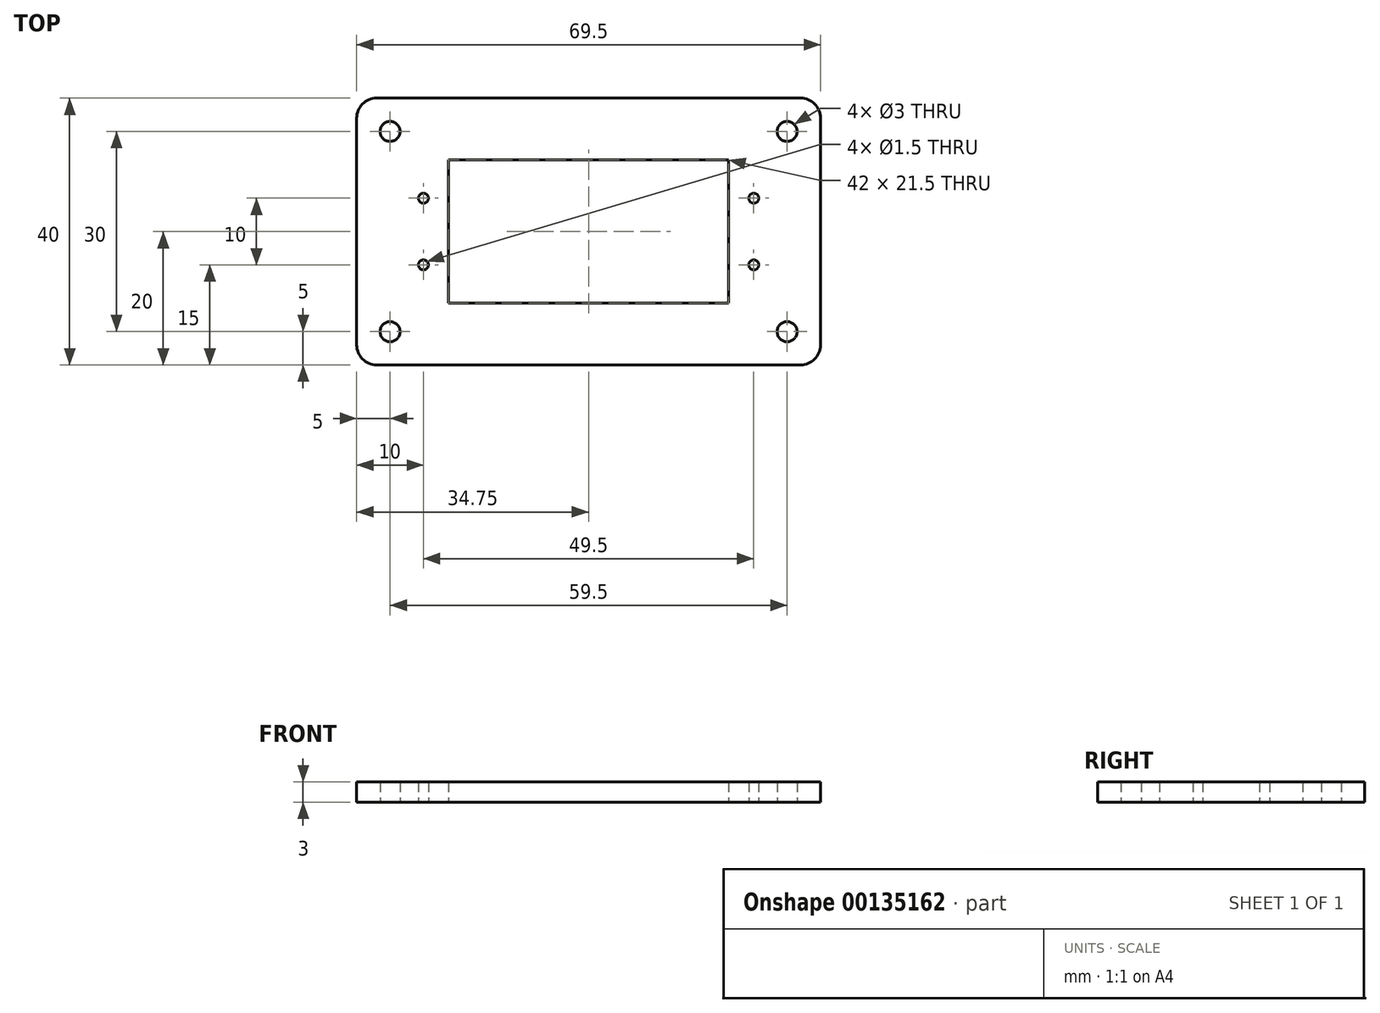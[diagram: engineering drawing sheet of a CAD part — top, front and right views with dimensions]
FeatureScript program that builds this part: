
annotation { "Feature Type Name" : "Feature", "Feature Type Description" : "" }
export const myFeature = defineFeature(function(context is Context, id is Id, definition is map)
    precondition{}
    {
        {
            var Q0;
            Q0=qCreatedBy(makeId("Top.planeOp"),FACE);
            var sketch = newSketch(context, id + "F0", { "sketchPlane" : qUnion([Q0])});
            skLineSegment(sketch, "E0.bottom", {"start": v(21, -10.75) * mm, "end": v(-21, -10.75) * mm});
            skLineSegment(sketch, "E0.top", {"start": v(21, 10.75) * mm, "end": v(-21, 10.75) * mm});
            skLineSegment(sketch, "E0.left", {"start": v(21, -10.75) * mm, "end": v(21, 10.75) * mm});
            skLineSegment(sketch, "E0.right", {"start": v(-21, -10.75) * mm, "end": v(-21, 10.75) * mm});
            skPoint(sketch, "E0.middle", {"position": v(0, 0) * mm});
            skLineSegment(sketch, "E1.bottom", {"start": v(24.75, -5) * mm, "end": v(-24.75, -5) * mm, "construction": true});
            skLineSegment(sketch, "E1.top", {"start": v(24.75, 5) * mm, "end": v(-24.75, 5) * mm, "construction": true});
            skLineSegment(sketch, "E1.left", {"start": v(24.75, -5) * mm, "end": v(24.75, 5) * mm, "construction": true});
            skLineSegment(sketch, "E1.right", {"start": v(-24.75, -5) * mm, "end": v(-24.75, 5) * mm, "construction": true});
            skLineSegment(sketch, "E2.bottom", {"start": v(34.75, -20) * mm, "end": v(-34.75, -20) * mm});
            skLineSegment(sketch, "E2.top", {"start": v(34.75, 20) * mm, "end": v(-34.75, 20) * mm});
            skLineSegment(sketch, "E2.left", {"start": v(34.75, -20) * mm, "end": v(34.75, 20) * mm});
            skLineSegment(sketch, "E2.right", {"start": v(-34.75, -20) * mm, "end": v(-34.75, 20) * mm});
            skLineSegment(sketch, "E3.bottom", {"start": v(-34.75, 20) * mm, "end": v(-29.75, 20) * mm, "construction": true});
            skLineSegment(sketch, "E3.top", {"start": v(-34.75, 15) * mm, "end": v(-29.75, 15) * mm, "construction": true});
            skLineSegment(sketch, "E3.left", {"start": v(-34.75, 20) * mm, "end": v(-34.75, 15) * mm, "construction": true});
            skLineSegment(sketch, "E3.right", {"start": v(-29.75, 20) * mm, "end": v(-29.75, 15) * mm, "construction": true});
            skLineSegment(sketch, "E4.bottom", {"start": v(34.75, 20) * mm, "end": v(29.75, 20) * mm, "construction": true});
            skLineSegment(sketch, "E4.top", {"start": v(34.75, 15) * mm, "end": v(29.75, 15) * mm, "construction": true});
            skLineSegment(sketch, "E4.left", {"start": v(34.75, 20) * mm, "end": v(34.75, 15) * mm, "construction": true});
            skLineSegment(sketch, "E4.right", {"start": v(29.75, 20) * mm, "end": v(29.75, 15) * mm, "construction": true});
            skLineSegment(sketch, "E5.bottom", {"start": v(-34.75, -20) * mm, "end": v(-29.75, -20) * mm, "construction": true});
            skLineSegment(sketch, "E5.top", {"start": v(-34.75, -15) * mm, "end": v(-29.75, -15) * mm, "construction": true});
            skLineSegment(sketch, "E5.left", {"start": v(-34.75, -20) * mm, "end": v(-34.75, -15) * mm, "construction": true});
            skLineSegment(sketch, "E5.right", {"start": v(-29.75, -20) * mm, "end": v(-29.75, -15) * mm, "construction": true});
            skLineSegment(sketch, "E6.bottom", {"start": v(34.75, -20) * mm, "end": v(29.75, -20) * mm, "construction": true});
            skLineSegment(sketch, "E6.top", {"start": v(34.75, -15) * mm, "end": v(29.75, -15) * mm, "construction": true});
            skLineSegment(sketch, "E6.left", {"start": v(34.75, -20) * mm, "end": v(34.75, -15) * mm, "construction": true});
            skLineSegment(sketch, "E6.right", {"start": v(29.75, -20) * mm, "end": v(29.75, -15) * mm, "construction": true});
            skCircle(sketch, "E7", {"center": v(-29.75, 15) * mm, "radius": 1.5 * mm});
            skCircle(sketch, "E8", {"center": v(29.75, 15) * mm, "radius": 1.5 * mm});
            skCircle(sketch, "E9", {"center": v(-29.75, -15) * mm, "radius": 1.5 * mm});
            skCircle(sketch, "E10", {"center": v(29.75, -15) * mm, "radius": 1.5 * mm});
            skCircle(sketch, "E11", {"center": v(-24.75, 5) * mm, "radius": 0.75 * mm});
            skCircle(sketch, "E12", {"center": v(24.75, 5) * mm, "radius": 0.75 * mm});
            skCircle(sketch, "E13", {"center": v(-24.75, -5) * mm, "radius": 0.75 * mm});
            skCircle(sketch, "E14", {"center": v(24.75, -5) * mm, "radius": 0.75 * mm});
            skSolve(sketch);
        }
        {
            var Q0;
            Q0=makeQuery(id+"F0.imprint","IMPRINT",FACE,{"disambiguationData":[TD([[makeQuery(id+"F0.imprint","IMPRINT",EDGE,{"derivedFrom":sQuery(id+"F0.wireOp",EDGE,"E0.bottom")}),1.0]])]});
            extrude(context, id + "F1", {"entities" : qUnion([Q0]), "depth" : 3 * mm});
        }
        {
            var Q0;
            Q0=makeQuery(id+"F1.opExtrude","SWEPT_EDGE",EDGE,{"disambiguationData":[OSD([sQuery(id+"F0.wireOp",EDGE,"E2.bottom"),sQuery(id+"F0.wireOp",EDGE,"E2.right")])]});
            var Q1;
            Q1=makeQuery(id+"F1.opExtrude","SWEPT_EDGE",EDGE,{"disambiguationData":[OSD([sQuery(id+"F0.wireOp",EDGE,"E2.bottom"),sQuery(id+"F0.wireOp",EDGE,"E2.left")])]});
            var Q2;
            Q2=makeQuery(id+"F1.opExtrude","SWEPT_EDGE",EDGE,{"disambiguationData":[OSD([sQuery(id+"F0.wireOp",EDGE,"E2.top"),sQuery(id+"F0.wireOp",EDGE,"E2.left")])]});
            var Q3;
            Q3=makeQuery(id+"F1.opExtrude","SWEPT_EDGE",EDGE,{"disambiguationData":[OSD([sQuery(id+"F0.wireOp",EDGE,"E2.top"),sQuery(id+"F0.wireOp",EDGE,"E2.right")])]});
            fillet(context, id + "F2", {"entities" : qUnion([Q0, Q1, Q2, Q3]), "radius" : 3 * mm, "tangentPropagation" : true, "allowEdgeOverflow" : false});
        }
    });
